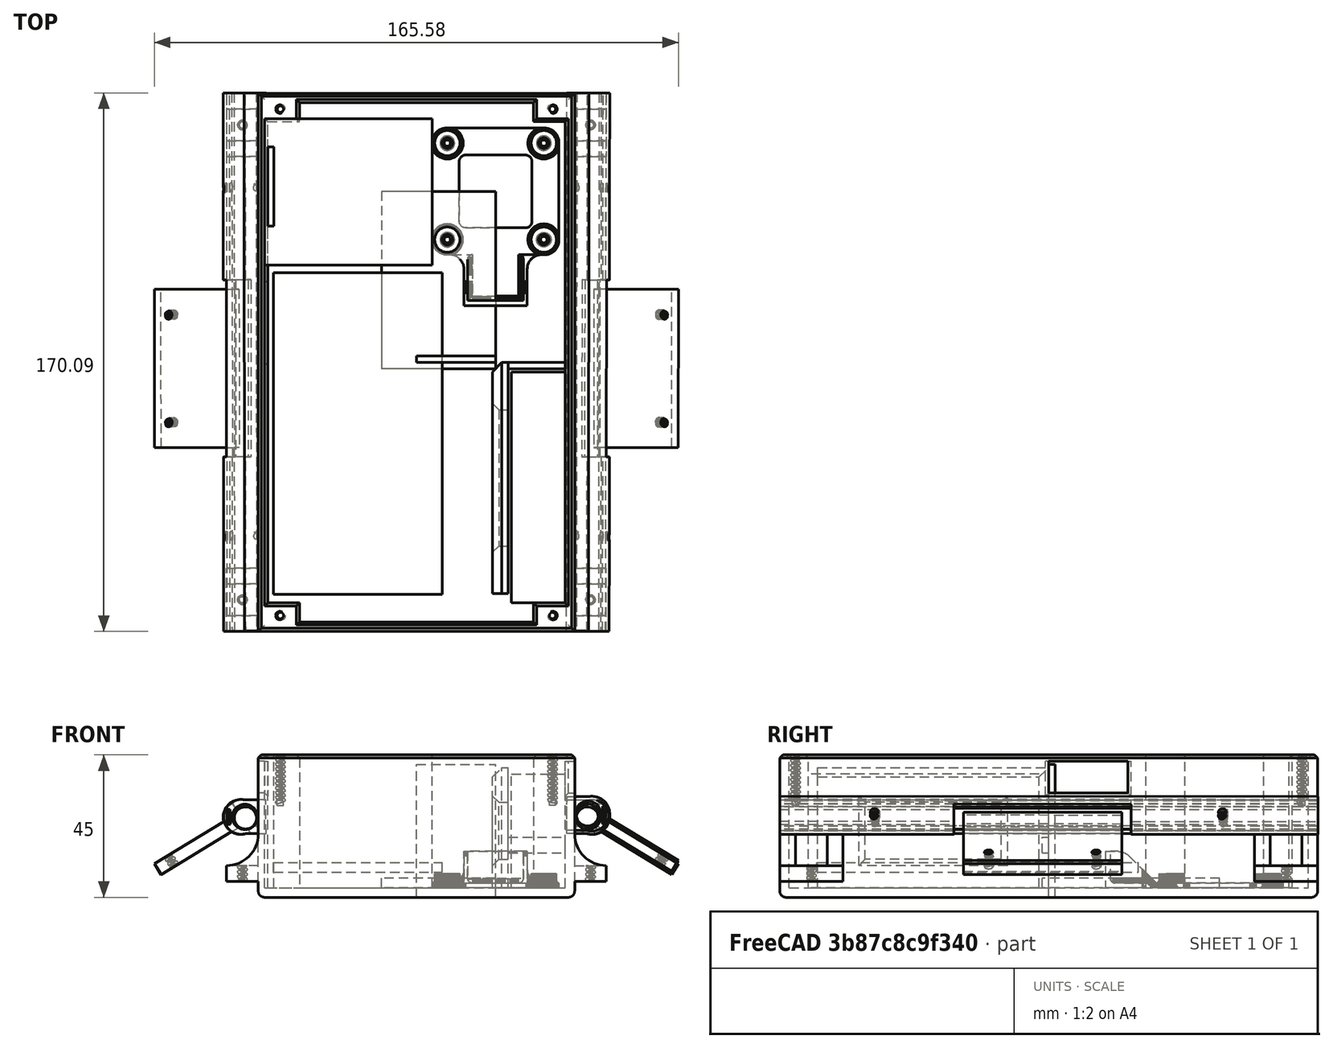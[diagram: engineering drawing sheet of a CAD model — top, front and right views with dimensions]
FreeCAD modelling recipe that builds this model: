
FCSTD DOCUMENT  (FreeCAD 0.19R)
Label: merged-carcasa-reducido
License: Creative Commons Attribution-NonCommercial-ShareAlike 4.0
LicenseURL: https://creativecommons.org/licenses/by-nc-sa/4.0/
objects: Part::Box×24, Part::Cut×18, Part::Fuse×18, Part::Feature×14, Part::Chamfer×9, Part::Mirroring×8, Sketcher::SketchObject×4, Part::Extrusion×4, Part::Cylinder×3, Part::Compound×3, App::DocumentObjectGroup×3, Part::MultiFuse×2, Part::Fillet×2, PartDesign::FeatureBase×1, PartDesign::Body×1, Mesh::Feature×1, App::LinkGroup×1, Part::Refine×1
note: 112 computed .brp shape members not serialized (recipe doc carries the construction recipe); baked Part::Feature solids carry a one-line shape summary decoded from their .brp

FEATURE [Sketcher::SketchObject] Sketch  label="case-taladros"
  FullyConstrained = true
  MapMode = 5
  Support = -> [XY_Plane]
  sketch-geometry (4):
    g0: LineSegment StartX=-50 StartY=85 StartZ=0 EndX=50 EndY=85 EndZ=0
    g1: LineSegment StartX=50 StartY=85 StartZ=0 EndX=50 EndY=-85 EndZ=0
    g2: LineSegment StartX=50 StartY=-85 StartZ=0 EndX=-50 EndY=-85 EndZ=0
    g3: LineSegment StartX=-50 StartY=-85 StartZ=0 EndX=-50 EndY=85 EndZ=0
  constraints (10):
    c: Coincident(g0,g1)
    c: Coincident(g1,g2)
    c: Coincident(g2,g3)
    c: Coincident(g3,g0)
    c: Horizontal(g2)
    c: Vertical(g1)
    c: Symmetric(g0,g0,g-2)
    c: Symmetric(g2,g0,g-1)
    c: DistanceY(g3,g3) = 170
    c: DistanceX(g0,g0) = 100
FEATURE [Part::Box] Box001  label="vaciado"
  AttacherType = Attacher::AttachEngine3D
  Height = 42
  Length = 94
  Placement = pos=(-47,-76,3) rot=(0,0,1;0rad)
  Width = 152
FEATURE [Sketcher::SketchObject] Sketch008  label="tapa-taladros"
  FullyConstrained = true
  MapMode = 5
  sketch-geometry (4):
    g0: LineSegment StartX=-49 StartY=84 StartZ=0 EndX=49 EndY=84 EndZ=0
    g1: LineSegment StartX=49 StartY=84 StartZ=0 EndX=49 EndY=-84 EndZ=0
    g2: LineSegment StartX=49 StartY=-84 StartZ=0 EndX=-49 EndY=-84 EndZ=0
    g3: LineSegment StartX=-49 StartY=-84 StartZ=0 EndX=-49 EndY=84 EndZ=0
  constraints (10):
    c: Coincident(g0,g1)
    c: Coincident(g1,g2)
    c: Coincident(g2,g3)
    c: Coincident(g3,g0)
    c: Horizontal(g2)
    c: Vertical(g1)
    c: Symmetric(g0,g0,g-2)
    c: Symmetric(g2,g0,g-1)
    c: DistanceY(g3,g3) = 168
    c: DistanceX(g0,g0) = 98
FEATURE [Part::Box] Box010  label="restriccion-lipo"
  AttacherType = Attacher::AttachEngine3D
  Height = 38
  Length = 5
  Placement = pos=(17,-75,5) rot=(0,0,1;0rad)
  Width = 73
FEATURE [Part::Box] Box011  label="restriccion-lipo001"
  AttacherType = Attacher::AttachEngine3D
  Height = 18
  Length = 7
  Placement = pos=(16,-60,14) rot=(0,0,1;0rad)
  Width = 43
FEATURE [Part::Cut] Cut028
  Base = -> Box010
  Refine = true
  Tool = -> Box011
FEATURE [Part::Chamfer] Chamfer002
  Base = -> Cut028
  Edges = 2 edges r=3: [Edge2,Edge4]
FEATURE [Part::Chamfer] Chamfer003
  Base = -> Chamfer002
  Edges = 4 edges r=2: [Edge5,Edge6,Edge7,Edge8]
FEATURE [Part::Box] Box012  label="Cube004"
  AttacherType = Attacher::AttachEngine3D
  Height = 5
  Length = 20
  Placement = pos=(20,-4,16) rot=(0,0,1;0rad)
  Width = 2
FEATURE [Part::Fuse] Fusion001032  label="rejillas-lipo"
  Base = -> Chamfer003
  Placement = pos=(7,2,-2) rot=(0,0,1;0rad)
  Refine = true
  Tool = -> Box012
FEATURE [Part::Box] Box015  label="Cubo002"
  AttacherType = Attacher::AttachEngine3D
  Height = 4
  Length = 50
  Placement = pos=(-25,22,-7.5) rot=(0,0,1;0rad)
  Width = 30
FEATURE [Part::Box] Box016  label="cubo-corte"
  AttacherType = Attacher::AttachEngine3D
  Height = 20
  Length = 56
  Placement = pos=(-145,75,-20) rot=(0,0,1;0rad)
  Width = 16
FEATURE [Part::Cylinder] Cylinder007  label="Cilindro-movil"
  Angle = 360
  AttacherType = Attacher::AttachEngine3D
  Height = 170
  Placement = pos=(-200,92,-6) rot=(0,1,0;1.5708rad)
  Radius = 3.5
FEATURE [Part::Feature] Fusion001034  label="Rosca macho012"
  Placement = pos=(-17,27,-10) rot=(0,0,1;0rad)
  shape: bbox 3.919 x 4.387 x 44 mm, 35 faces (baked)
FEATURE [Part::Feature] Fusion001035  label="Rosca macho013"
  Placement = pos=(17,27,-10) rot=(0,0,1;0rad)
  shape: bbox 3.919 x 4.387 x 44 mm, 35 faces (baked)
FEATURE [Part::MultiFuse] Fusion001036
  Refine = true
  Shapes = -> [Fusion001034,Fusion001035]
FEATURE [Part::Cut] Cut030  label="Soporte_eje001"
  Base = -> Box015
  Placement = pos=(-117,38,0) rot=(0,0,1;0rad)
  Refine = true
  Tool = -> Fusion001036
FEATURE [Part::Feature] Fusion001037  label="Rosca macho014"
  Placement = pos=(-170,93.75,-8.78) rot=(0.819304,0.219813,-0.52955;0.936369rad)
  shape: bbox 4.221 x 33 x 32.52 mm, 35 faces (baked)
FEATURE [Part::Feature] Fusion001038  label="Rosca macho015"
  Placement = pos=(-60,93.75,-8.78) rot=(0.819304,0.219813,-0.52955;0.936369rad)
  shape: bbox 4.221 x 33 x 32.52 mm, 35 faces (baked)
FEATURE [Part::Fuse] Fusion001033  label="roscas002"
  Base = -> Fusion001037
  Refine = true
  Tool = -> Fusion001038
FEATURE [Part::Fuse] Fusion001039  label="cilindro-movil001"
  Base = -> Cut030
  Refine = true
  Tool = -> Cylinder007
FEATURE [Sketcher::SketchObject] Sketch009
  FullyConstrained = false
  MapMode = 5
  Placement = pos=(0,0,0) rot=(0.57735,0.57735,0.57735;2.0944rad)
  Support = -> [YZ_Plane004]
  sketch-geometry (9):
    g0: ArcOfCircle CenterX=0 CenterY=0 CenterZ=0 NormalX=0 NormalY=0 NormalZ=1 AngleXU=0 Radius=5.5 StartAngle=6.08579 EndAngle=9.70025
    g1: Circle CenterX=0 CenterY=-1.19343 CenterZ=0 NormalX=0 NormalY=0 NormalZ=1 AngleXU=0 Radius=4
    g2: LineSegment StartX=-2.36 StartY=4.37566 StartZ=0 EndX=2.36 EndY=4.37566 EndZ=0
    g3: LineSegment StartX=2.36 StartY=4.37566 StartZ=0 EndX=2.36 EndY=3.44566 EndZ=0
    g4: LineSegment StartX=2.36 StartY=3.44566 StartZ=0 EndX=-2.36 EndY=3.44566 EndZ=0
    g5: LineSegment StartX=-2.36 StartY=3.44566 StartZ=0 EndX=-2.36 EndY=4.37566 EndZ=0
    g6: LineSegment StartX=-5.29263 StartY=-1.49602 StartZ=0 EndX=-5.29263 EndY=-8 EndZ=0
    g7: LineSegment StartX=-5.29263 StartY=-8 StartZ=0 EndX=5.39319 EndY=-8 EndZ=0
    g8: LineSegment StartX=5.39319 StartY=-8 StartZ=0 EndX=5.39319 EndY=-1.07864 EndZ=0
  constraints (21):
    c: Coincident(g0,g-1)
    c: Coincident(g2,g3)
    c: Coincident(g3,g4)
    c: Coincident(g4,g5)
    c: Coincident(g5,g2)
    c: Horizontal(g4)
    c: Vertical(g3)
    c: Vertical(g5)
    c: Symmetric(g2,g2,g-2)
    c: PointOnObject(g1,g-2)
    c: Radius(g0) = 5.5
    c: Radius(g1) = 4
    c: DistanceY(g5,g5) = 0.93
    c: DistanceX(g2,g2) = 4.72
    c: Coincident(g6,g7)
    c: Coincident(g7,g8)
    c: Horizontal(g7)
    c: Vertical(g6)
    c: Vertical(g8)
    c: Coincident(g0,g8)
    c: Coincident(g6,g0)
FEATURE [Part::Extrusion] Extrude003  label="cilindro-fijo001"
  Base = -> Sketch009
  Dir = (1,-1e-16,1e-16)
  DirMode = 2
  FaceMakerClass = Part::FaceMakerBullseye
  LengthFwd = 170
  LengthRev = 0
  Placement = pos=(-200,91,-5) rot=(1,0,0;1.02974rad)
  Solid = true
  Symmetric = false
FEATURE [Part::Cut] Cut029
  Base = -> Extrude003
  Refine = true
  Tool = -> Fusion001033
FEATURE [Part::Cut] Cut031  label="fijacion-brazo"
  Base = -> Cut029
  Refine = true
  Tool = -> Box016
FEATURE [Part::Compound] Compound  label="brazo-mejorados"
  Links = -> [Cut031,Fusion001039]
  Placement = pos=(136,115,-16.54) rot=(0.259987,0.259987,0.929954;1.64236rad)
FEATURE [Part::Mirroring] Part__Mirroring014  label="brazo-mejorados (Mirror #13)"
  Base = (0,0,0)
  Normal = (1,0,0)
  Source = -> Compound
FEATURE [Part::Extrusion] Extrude  label="carcasa-extruida"
  Base = -> Sketch
  Dir = (0,0,1)
  DirMode = 2
  FaceMakerClass = Part::FaceMakerBullseye
  LengthFwd = 45
  LengthRev = 0
  Solid = true
  Symmetric = false
FEATURE [Part::Box] Box019  label="vaciado001"
  AttacherType = Attacher::AttachEngine3D
  Height = 42
  Length = 74
  Placement = pos=(-37,-82,3) rot=(0,0,1;0rad)
  Width = 164
FEATURE [Part::Cut] Cut
  Base = -> Extrude
  Refine = true
  Tool = -> Box001
FEATURE [Part::Cut] Cut034
  Base = -> Cut
  Refine = true
  Tool = -> Box019
FEATURE [Part::Chamfer] Chamfer
  Base = -> Cut034
  Edges = 4 edges r=1: [Edge4,Edge7,Edge10,Edge12]
FEATURE [Part::Chamfer] Chamfer005
  Base = -> Chamfer
  Edges = 12 edges r=1: [Edge20,Edge21,Edge22,Edge23,Edge24,Edge25,Edge26,Edge27,Edge28,Edge29,Edge30,Edge31]
FEATURE [Part::Fillet] Fillet  label="carcasa-chaflanada"
  Base = -> Chamfer005
  Edges = 4 edges r=2: [Edge75,Edge77,Edge79,Edge80]
FEATURE [Part::Fuse] Fusion001040  label="brazos-v2"
  Base = -> Compound
  Placement = pos=(0,0,-1) rot=(0,0,1;0rad)
  Refine = true
  Tool = -> Part__Mirroring014
FEATURE [Part::Extrusion] Extrude004
  Base = -> Sketch008
  Dir = (0,0,1)
  DirMode = 2
  FaceMakerClass = Part::FaceMakerBullseye
  LengthFwd = 25
  LengthRev = 0
  Placement = pos=(0,0,45) rot=(0,0,1;0rad)
  Solid = true
  Symmetric = false
FEATURE [Part::Chamfer] Chamfer006  label="tapa"
  Base = -> Extrude004
  Edges = 4 edges r=2: [Edge4,Edge7,Edge10,Edge12]
FEATURE [Part::Box] Box  label="Cube"
  AttacherType = Attacher::AttachEngine3D
  Height = 5
  Length = 10
  Width = 20
FEATURE [Part::Box] Box020  label="Cube001"
  AttacherType = Attacher::AttachEngine3D
  Height = 50
  Length = 5
  Placement = pos=(-5,0,0) rot=(0,0,1;0rad)
  Width = 20
FEATURE [Part::Box] Box002  label="Cube002"
  AttacherType = Attacher::AttachEngine3D
  Height = 50
  Length = 5
  Placement = pos=(-5,0,0) rot=(0,0,1;0rad)
  Width = 20
FEATURE [Part::Box] Box003  label="Cube003"
  AttacherType = Attacher::AttachEngine3D
  Height = 20
  Length = 10
  Placement = pos=(0,5,5) rot=(0,0,1;0rad)
  Width = 10
FEATURE [Part::Cylinder] Cylinder
  Angle = 360
  AttacherType = Attacher::AttachEngine3D
  Height = 6
  Placement = pos=(5,10,0) rot=(0,0,1;0rad)
  Radius = 0.5
FEATURE [Part::Fuse] Fusion001047
  Base = -> Box
  Refine = true
  Tool = -> Box020
FEATURE [Part::Fillet] Fillet001
  Base = -> Fusion001047
  Edges = 1 edges r=9.99: [Edge5]
FEATURE [Part::Cut] Cut035
  Base = -> Fillet001
  Refine = true
  Tool = -> Box002
FEATURE [Part::Cut] Cut001
  Base = -> Cut035
  Refine = true
  Tool = -> Box003
FEATURE [Part::Cut] Cut002  label="acople"
  Base = -> Cut001
  Refine = true
  Tool = -> Cylinder
FEATURE [Part::Feature] Fusion001001  label="Rosca macho002"
  Placement = pos=(5,10,-9) rot=(0,0,1;0rad)
  shape: bbox 3.919 x 4.387 x 44 mm, 35 faces (baked)
FEATURE [Part::Cut] Cut003  label="acople-roscado"
  Base = -> Cut002
  Placement = pos=(50,-85,5) rot=(0,0,1;0rad)
  Refine = true
  Tool = -> Fusion001001
FEATURE [Part::Mirroring] Part__Mirroring021  label="acople-roscado (Mirror #7)"
  Base = (0,0,0)
  Normal = (1,0,0)
  Source = -> Cut003
FEATURE [Part::Fuse] Fusion001048
  Base = -> Cut003
  Refine = true
  Tool = -> Part__Mirroring021
FEATURE [Part::Mirroring] Part__Mirroring022  label="Fusion001048 (Mirror #8)"
  Base = (0,0,0)
  Normal = (0,1,0)
  Source = -> Fusion001048
FEATURE [Part::Fuse] Fusion001049  label="acoples-flotador"
  Base = -> Fusion001048
  Refine = true
  Tool = -> Part__Mirroring022
FEATURE [Part::Feature] Compound002  label="simple-rosca"
  Placement = pos=(43,-80,30) rot=(0,0,1;0rad)
  shape: bbox 3.919 x 4.387 x 44 mm, 65 faces (baked)
FEATURE [Part::Mirroring] Part__Mirroring023  label="simple-rosca (Mirror #7)"
  Base = (0,0,0)
  Normal = (1,0,0)
  Source = -> Compound002
FEATURE [Part::Fuse] Fusion001050
  Base = -> Compound002
  Refine = true
  Tool = -> Part__Mirroring023
FEATURE [Part::Mirroring] Part__Mirroring024  label="roscas-4"
  Base = (0,0,0)
  Normal = (0,1,0)
  Source = -> Fusion001050
FEATURE [Part::Fuse] Fusion001051  label="roscas-carcasa"
  Base = -> Fusion001050
  Refine = true
  Tool = -> Part__Mirroring024
FEATURE [Part::Feature] Compound003  label="simple-rosca001"
  Placement = pos=(43,-80,30) rot=(0,0,1;0rad)
  shape: bbox 3.919 x 4.387 x 44 mm, 65 faces (baked)
FEATURE [Part::Mirroring] Part__Mirroring025  label="simple-rosca (Mirror #7)001"
  Base = (0,0,0)
  Normal = (1,0,0)
  Source = -> Compound003
FEATURE [Part::Fuse] Fusion001052
  Base = -> Compound003
  Refine = true
  Tool = -> Part__Mirroring025
FEATURE [Part::Mirroring] Part__Mirroring026  label="roscas-005"
  Base = (0,0,0)
  Normal = (0,1,0)
  Source = -> Fusion001052
FEATURE [Part::Fuse] Fusion001053  label="roscas-tapa"
  Base = -> Fusion001052
  Refine = true
  Tool = -> Part__Mirroring026
FEATURE [Part::Cut] Cut036  label="carcasa-roscada-15mm"
  Base = -> Fillet
  Refine = true
  Tool = -> Fusion001051
FEATURE [Part::Box] Box021  label="agujeros-new"
  AttacherType = Attacher::AttachEngine3D
  Height = 10
  Length = 10
  Placement = pos=(43,0,33) rot=(0,0,1;0rad)
  Width = 25
FEATURE [Part::Mirroring] Part__Mirroring027  label="agujeros-new (Mirror #11)"
  Base = (0,0,0)
  Normal = (1,0,0)
  Source = -> Box021
FEATURE [Part::Fuse] Fusion001054  label="agujeros-rectangulares"
  Base = -> Box021
  Refine = true
  Tool = -> Part__Mirroring027
FEATURE [Part::Box] Box024  label="receptor-space"
  AttacherType = Attacher::AttachEngine3D
  Height = 42
  Length = 25
  Placement = pos=(-47,68,3) rot=(0,0,-1;1.5708rad)
  Width = 2
FEATURE [PartDesign::FeatureBase] BaseFeature
  BaseFeature = -> Box024
FEATURE [PartDesign::Body] Body  label="carcasa-boceto"
  BaseFeature = -> Box024
  Group = -> [BaseFeature,Sketch]
  Origin = -> Origin
  Tip = -> BaseFeature
FEATURE [Part::Box] Box025  label="vaciado002"
  AttacherType = Attacher::AttachEngine3D
  Height = 24
  Length = 94
  Placement = pos=(-47,-76,44) rot=(0,0,1;0rad)
  Width = 152
FEATURE [Part::Fuse] Fusion
  Base = -> Fusion001049
  Refine = true
  Tool = -> Cut036
FEATURE [Part::Fuse] Fusion001055
  Base = -> Fusion001040
  Refine = true
  Tool = -> Fusion
FEATURE [Part::Cut] Cut039  label="carcasa-fusionada"
  Base = -> Fusion001055
  Refine = true
  Tool = -> Fusion001054
FEATURE [Part::Chamfer] Chamfer007
  Base = -> Cut039
  Edges = 3 edges r=1: [Edge393,Edge397,Edge398]
FEATURE [Part::Chamfer] Chamfer008
  Base = -> Chamfer007
  Edges = 3 edges r=1: [Edge341,Edge342,Edge344]
FEATURE [Part::Fuse] Fusion001056  label="carcasa-merged"
  Base = -> Fusion001032
  Refine = true
  Tool = -> Chamfer008
FEATURE [Part::Compound] Compound004  label="carcasa-compound"
  Links = -> [Fusion001056]
FEATURE [Part::Box] Box026  label="Cubo003"
  AttacherType = Attacher::AttachEngine3D
  Height = 4
  Length = 50
  Placement = pos=(-25,22,-7.5) rot=(0,0,1;0rad)
  Width = 30
FEATURE [Part::Box] Box027  label="cubo-corte001"
  AttacherType = Attacher::AttachEngine3D
  Height = 20
  Length = 56
  Placement = pos=(-145,75,-20) rot=(0,0,1;0rad)
  Width = 16
FEATURE [Part::Cylinder] Cylinder008  label="Cilindro-movil001"
  Angle = 360
  AttacherType = Attacher::AttachEngine3D
  Height = 170
  Placement = pos=(-200,92,-6) rot=(0,1,0;1.5708rad)
  Radius = 3.5
FEATURE [Part::Feature] Fusion001058  label="Rosca macho016"
  Placement = pos=(-17,27,-10) rot=(0,0,1;0rad)
  shape: bbox 3.919 x 4.387 x 44 mm, 35 faces (baked)
FEATURE [Part::Feature] Fusion001059  label="Rosca macho017"
  Placement = pos=(17,27,-10) rot=(0,0,1;0rad)
  shape: bbox 3.919 x 4.387 x 44 mm, 35 faces (baked)
FEATURE [Part::MultiFuse] Fusion001060
  Refine = true
  Shapes = -> [Fusion001058,Fusion001059]
FEATURE [Part::Cut] Cut041  label="Soporte_eje002"
  Base = -> Box026
  Placement = pos=(-117,38,0) rot=(0,0,1;0rad)
  Refine = true
  Tool = -> Fusion001060
FEATURE [Part::Feature] Fusion001061  label="Rosca macho018"
  Placement = pos=(-170,93.75,-8.78) rot=(0.819304,0.219813,-0.52955;0.936369rad)
  shape: bbox 4.221 x 33 x 32.52 mm, 35 faces (baked)
FEATURE [Part::Feature] Fusion001062  label="Rosca macho019"
  Placement = pos=(-60,93.75,-8.78) rot=(0.819304,0.219813,-0.52955;0.936369rad)
  shape: bbox 4.221 x 33 x 32.52 mm, 35 faces (baked)
FEATURE [Part::Fuse] Fusion001057  label="roscas003"
  Base = -> Fusion001061
  Refine = true
  Tool = -> Fusion001062
FEATURE [Part::Fuse] Fusion001063  label="cilindro-movil002"
  Base = -> Cut041
  Refine = true
  Tool = -> Cylinder008
FEATURE [Sketcher::SketchObject] Sketch010
  FullyConstrained = false
  MapMode = 5
  Placement = pos=(0,0,0) rot=(0.57735,0.57735,0.57735;2.0944rad)
  Support = -> [YZ_Plane005]
  sketch-geometry (9):
    g0: ArcOfCircle CenterX=0 CenterY=0 CenterZ=0 NormalX=0 NormalY=0 NormalZ=1 AngleXU=0 Radius=5.5 StartAngle=6.08579 EndAngle=9.70025
    g1: Circle CenterX=0 CenterY=-1.19343 CenterZ=0 NormalX=0 NormalY=0 NormalZ=1 AngleXU=0 Radius=4
    g2: LineSegment StartX=-2.36 StartY=4.37566 StartZ=0 EndX=2.36 EndY=4.37566 EndZ=0
    g3: LineSegment StartX=2.36 StartY=4.37566 StartZ=0 EndX=2.36 EndY=3.44566 EndZ=0
    g4: LineSegment StartX=2.36 StartY=3.44566 StartZ=0 EndX=-2.36 EndY=3.44566 EndZ=0
    g5: LineSegment StartX=-2.36 StartY=3.44566 StartZ=0 EndX=-2.36 EndY=4.37566 EndZ=0
    g6: LineSegment StartX=-5.29263 StartY=-1.49602 StartZ=0 EndX=-5.29263 EndY=-8 EndZ=0
    g7: LineSegment StartX=-5.29263 StartY=-8 StartZ=0 EndX=5.39319 EndY=-8 EndZ=0
    g8: LineSegment StartX=5.39319 StartY=-8 StartZ=0 EndX=5.39319 EndY=-1.07864 EndZ=0
  constraints (21):
    c: Coincident(g0,g-1)
    c: Coincident(g2,g3)
    c: Coincident(g3,g4)
    c: Coincident(g4,g5)
    c: Coincident(g5,g2)
    c: Horizontal(g4)
    c: Vertical(g3)
    c: Vertical(g5)
    c: Symmetric(g2,g2,g-2)
    c: PointOnObject(g1,g-2)
    c: Radius(g0) = 5.5
    c: Radius(g1) = 4
    c: DistanceY(g5,g5) = 0.93
    c: DistanceX(g2,g2) = 4.72
    c: Coincident(g6,g7)
    c: Coincident(g7,g8)
    c: Horizontal(g7)
    c: Vertical(g6)
    c: Vertical(g8)
    c: Coincident(g0,g8)
    c: Coincident(g6,g0)
FEATURE [Part::Extrusion] Extrude005  label="cilindro-fijo002"
  Base = -> Sketch010
  Dir = (1,-1e-16,1e-16)
  DirMode = 2
  FaceMakerClass = Part::FaceMakerBullseye
  LengthFwd = 170
  LengthRev = 0
  Placement = pos=(-200,91,-5) rot=(1,0,0;1.02974rad)
  Solid = true
  Symmetric = false
FEATURE [Part::Cut] Cut040
  Base = -> Extrude005
  Refine = true
  Tool = -> Fusion001057
FEATURE [Part::Cut] Cut042  label="fijacion-brazo001"
  Base = -> Cut040
  Refine = true
  Tool = -> Box027
FEATURE [Part::Compound] Compound006  label="brazo-mejorados001"
  Links = -> [Cut042,Fusion001063]
  Placement = pos=(136,115,-16.54) rot=(0.259987,0.259987,0.929954;1.64236rad)
FEATURE [Mesh::Feature] Arduino_Bumper_0005  label="Arduino-uno-case"
  Placement = pos=(-19,-40,5) rot=(0,0,1;-1.5708rad)
FEATURE [Part::Box] Box028  label="restriccion-lipo002"
  AttacherType = Attacher::AttachEngine3D
  Height = 38
  Length = 5
  Placement = pos=(17,-75,5) rot=(0,0,1;0rad)
  Width = 73
FEATURE [Part::Box] Box029  label="restriccion-lipo003"
  AttacherType = Attacher::AttachEngine3D
  Height = 18
  Length = 7
  Placement = pos=(16,-60,14) rot=(0,0,1;0rad)
  Width = 43
FEATURE [Part::Box] Box030  label="Cube005"
  AttacherType = Attacher::AttachEngine3D
  Height = 5
  Length = 20
  Placement = pos=(20,-4,16) rot=(0,0,1;0rad)
  Width = 2
FEATURE [Part::Box] Box013  label="PDB-space"
  AttacherType = Attacher::AttachEngine3D
  Height = 3
  Length = 36
  Placement = pos=(25,54,3) rot=(0,0,1;3.14159rad)
  Width = 56
FEATURE [Part::Box] Box014  label="free-space"
  AttacherType = Attacher::AttachEngine3D
  Height = 42
  Length = 46.3
  Placement = pos=(-48,77,3) rot=(0,0,-1;1.5708rad)
  Width = 53
FEATURE [Part::Box] Box022  label="lipo-space"
  AttacherType = Attacher::AttachEngine3D
  Height = 36
  Length = 73
  Placement = pos=(30,-3,3) rot=(0,0,-1;1.5708rad)
  Width = 17
FEATURE [Part::Box] Box023  label="arduino-mega-space"
  AttacherType = Attacher::AttachEngine3D
  Height = 3
  Length = 53.3
  Placement = pos=(-45.15,-73.26,8) rot=(0,0,1;0rad)
  Width = 101.52
FEATURE [Part::Box] Box031  label="receptor-space001"
  AttacherType = Attacher::AttachEngine3D
  Height = 42
  Length = 25
  Placement = pos=(-47,68,3) rot=(0,0,-1;1.5708rad)
  Width = 2
FEATURE [Part::Feature] Compound001  label="pcb-support"
  Placement = pos=(25,54,3) rot=(0,0,1;3.14159rad)
  shape: bbox 40 x 56.1 x 12 mm, 27565 faces, 3 solids (baked)
FEATURE [Part::Feature] Compound007  label="arduino-mega-case-solid"
  Placement = pos=(-62,80,3) rot=(0,0,-1;1.5708rad)
  shape: bbox 57.6 x 106.6 x 5.8 mm, 182 faces (baked)
FEATURE [Part::Cut] Cut043
  Base = -> Box028
  Refine = true
  Tool = -> Box029
FEATURE [Part::Chamfer] Chamfer009
  Base = -> Cut043
  Edges = 2 edges r=3: [Edge2,Edge4]
FEATURE [Part::Chamfer] Chamfer010
  Base = -> Chamfer009
  Edges = 4 edges r=2: [Edge5,Edge6,Edge7,Edge8]
FEATURE [Part::Fuse] Fusion001064  label="rejillas-lipo001"
  Base = -> Chamfer010
  Placement = pos=(7,2,-2) rot=(0,0,1;0rad)
  Refine = true
  Tool = -> Box030
FEATURE [App::LinkGroup] LinkGroup  label="componentes-shell"
  ElementList = -> [Compound001,Box013,Box014,Fusion001064,Arduino_Bumper_0005,Compound007,Box022,Box023,Box031]
  LinkMode = 0
FEATURE [Part::Refine] Compound008  label="pcb-support001"
  Source = -> Compound001
FEATURE [App::DocumentObjectGroup] Group001  label="Componentes-interior"
  Group = -> [LinkGroup,Compound008,Box024]
FEATURE [App::DocumentObjectGroup] Group003  label="Carcasa-boceto-inicial"
  Group = -> [Body,YZ_Plane004]
FEATURE [Part::Feature] Compound009  label="carcasa-compound-simple"
  shape: bbox 165.6 x 170.1 x 47.45 mm, 385 faces, 3 solids (baked)
FEATURE [Part::Cut] Cut044
  Base = -> Chamfer006
  Refine = true
  Tool = -> Box025
FEATURE [Part::Cut] Cut045  label="Tapa"
  Base = -> Cut044
  Refine = true
  Tool = -> Fusion001053
FEATURE [App::DocumentObjectGroup] Group002  label="Tapa-Carcasa"
  Group = -> [Cut045]
